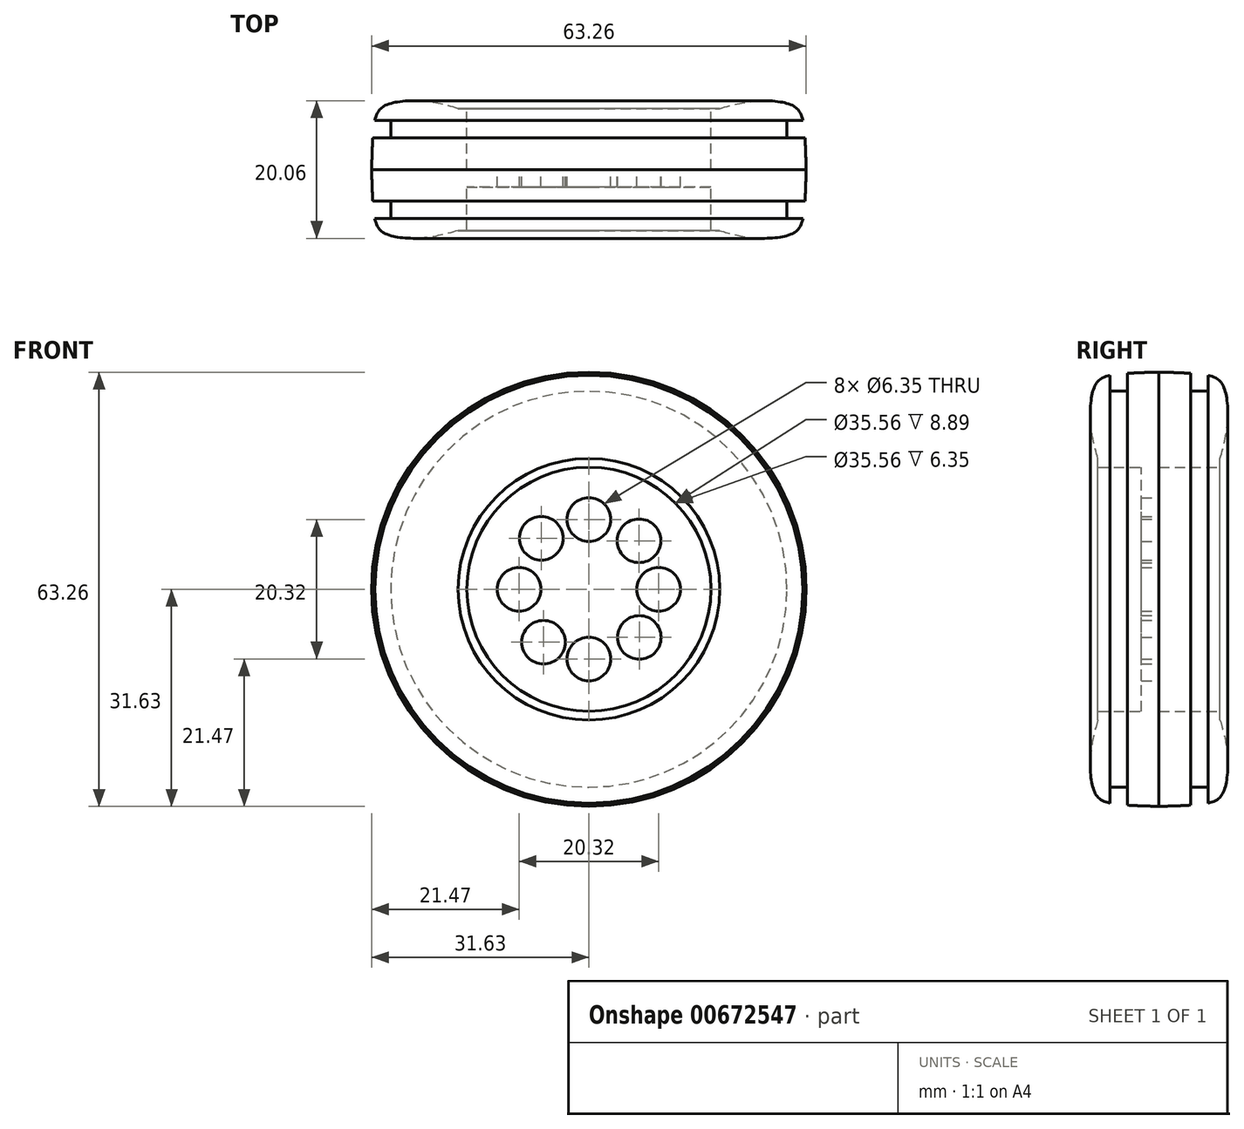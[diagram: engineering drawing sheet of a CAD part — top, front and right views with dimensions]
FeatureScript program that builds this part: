
annotation { "Feature Type Name" : "Feature", "Feature Type Description" : "" }
export const myFeature = defineFeature(function(context is Context, id is Id, definition is map)
    precondition{}
    {
        {
            var Q0;
            Q0=qCreatedBy(makeId("Front.planeOp"),FACE);
            var sketch = newSketch(context, id + "F0", { "sketchPlane" : qUnion([Q0])});
            skCircle(sketch, "E0", {"center": v(0, 0) * mm, "radius": 17.78 * mm});
            skCircle(sketch, "E1", {"center": v(0, 0) * mm, "radius": 19.05 * mm});
            skSolve(sketch);
        }
        {
            var Q0;
            Q0 = qSketchRegion(id + "F0", true);
            extrude(context, id + "F1", {"entities" : qUnion([Q0]), "endBound" : BoundingType.SYMMETRIC, "depth" : 17.78 * mm, "hasOffset" : true, "offsetDistance" : 25.4 * mm, "hasSecondDirection" : true, "secondDirectionOppositeDirection" : true, "secondDirectionDepth" : 25.4 * mm});
        }
        {
            var Q0;
            Q0=qCreatedBy(makeId("Front.planeOp"),FACE);
            var sketch = newSketch(context, id + "F2", { "sketchPlane" : qUnion([Q0])});
            skCircle(sketch, "E2", {"center": v(0, 0) * mm, "radius": 19.05 * mm});
            skCircle(sketch, "E3", {"center": v(0, 10.16) * mm, "radius": 3.18 * mm});
            skCircle(sketch, "E4.MirrorC", {"center": v(0, -10.16) * mm, "radius": 3.18 * mm});
            skCircle(sketch, "E5", {"center": v(-10.16, 0) * mm, "radius": 3.18 * mm});
            skCircle(sketch, "E6.MirrorC", {"center": v(10.16, 0) * mm, "radius": 3.18 * mm});
            skCircle(sketch, "E7", {"center": v(7.3, 7.06) * mm, "radius": 3.18 * mm});
            skCircle(sketch, "E8", {"center": v(-6.93, 7.43) * mm, "radius": 3.18 * mm});
            skCircle(sketch, "E9", {"center": v(-6.6, -7.72) * mm, "radius": 3.18 * mm});
            skCircle(sketch, "E10", {"center": v(7.34, -7.02) * mm, "radius": 3.18 * mm});
            skSolve(sketch);
        }
        {
            var Q0;
            Q0=makeQuery(id+"F2.imprint","IMPRINT",FACE,{"disambiguationData":[TD([[makeQuery(id+"F2.imprint","IMPRINT",EDGE,{"derivedFrom":sQuery(id+"F2.wireOp",EDGE,"E2")}),1.0]])]});
            extrude(context, id + "F3", {"entities" : qUnion([Q0]), "operationType" : NewBodyOperationType.ADD, "depth" : 2.54 * mm, "offsetDistance" : 25.4 * mm});
        }
        {
            var Q0;
            Q0=qCreatedBy(makeId("Right.planeOp"),FACE);
            var sketch = newSketch(context, id + "F4", { "sketchPlane" : qUnion([Q0])});
            skFitSpline(sketch, "E11", {"points": [v(8.9, 19.05) * mm, v(9.97, 24.24) * mm, v(9.61, 28.93) * mm, v(8.35, 30.73) * mm, v(4.74, 31.45) * mm, v(0, 31.63) * mm], "startDerivative": vector(6.3, 20.55) * mm, "endDerivative": vector(-21.7, 0.52) * mm});
            skFitSpline(sketch, "E12.MirrorCS", {"points": [v(-8.9, 19.05) * mm, v(-9.97, 24.24) * mm, v(-9.61, 28.93) * mm, v(-8.35, 30.73) * mm, v(-4.74, 31.45) * mm, v(0, 31.63) * mm], "startDerivative": vector(-6.3, 20.55) * mm, "endDerivative": vector(21.7, 0.52) * mm});
            skLineSegment(sketch, "E13", {"start": v(8.9, 19.05) * mm, "end": v(-8.9, 19.05) * mm});
            skLineSegment(sketch, "E14", {"start": v(7.13, 31.17) * mm, "end": v(7.13, 28.85) * mm});
            skLineSegment(sketch, "E15", {"start": v(7.13, 28.85) * mm, "end": v(4.59, 28.85) * mm});
            skLineSegment(sketch, "E16", {"start": v(4.59, 28.85) * mm, "end": v(4.59, 31.46) * mm});
            skLineSegment(sketch, "E17", {"start": v(4.59, 31.46) * mm, "end": v(3.9, 31.5) * mm});
            skLineSegment(sketch, "E18", {"start": v(3.9, 31.5) * mm, "end": v(3.9, 28.85) * mm});
            skLineSegment(sketch, "E19", {"start": v(3.9, 28.85) * mm, "end": v(1.37, 28.85) * mm});
            skLineSegment(sketch, "E20", {"start": v(1.37, 28.85) * mm, "end": v(1.37, 31.6) * mm});
            skLineSegment(sketch, "E21.MirrorCS", {"start": v(-1.37, 28.85) * mm, "end": v(-1.37, 31.6) * mm});
            skLineSegment(sketch, "E22.MirrorCS", {"start": v(-3.9, 28.85) * mm, "end": v(-1.37, 28.85) * mm});
            skLineSegment(sketch, "E23.MirrorCS", {"start": v(-3.9, 31.5) * mm, "end": v(-3.9, 28.85) * mm});
            skLineSegment(sketch, "E24.MirrorCS", {"start": v(-4.59, 28.85) * mm, "end": v(-4.59, 31.46) * mm});
            skLineSegment(sketch, "E25.MirrorCS", {"start": v(-7.13, 28.85) * mm, "end": v(-4.59, 28.85) * mm});
            skLineSegment(sketch, "E26.MirrorCS", {"start": v(-7.13, 31.17) * mm, "end": v(-7.13, 28.85) * mm});
            skSolve(sketch);
        }
        {
            var Q0;
            {var subQ0=sQuery(id+"F4.wireOp",EDGE,"E17");Q0=makeQuery(id+"F4.imprint","IMPRINT",FACE,{"disambiguationData":[TD([[makeQuery(id+"F4.imprint","IMPRINT",EDGE,{"derivedFrom":subQ0}),-1.0]])]});}
            var Q1;
            {var subQ2=sQuery(id+"F4.wireOp",EDGE,"E13");Q1=makeQuery(id+"F4.imprint","IMPRINT",FACE,{"disambiguationData":[TD([[makeQuery(id+"F4.imprint","IMPRINT",EDGE,{"derivedFrom":subQ2}),-1.0]])]});}
            var Q2;
            Q2=makeQuery(id+"F1.opExtrude","SWEPT_FACE",FACE,{"disambiguationData":[OSD([sQuery(id+"F0.wireOp",EDGE,"E1")])]});
            revolve(context, id + "F5", {"operationType" : NewBodyOperationType.ADD, "surfaceOperationType" : NewSurfaceOperationType.NEW, "entities" : qUnion([Q0, Q1]), "axis" : qUnion([Q2]), "revolveType" : RevolveType.FULL});
        }
    });
